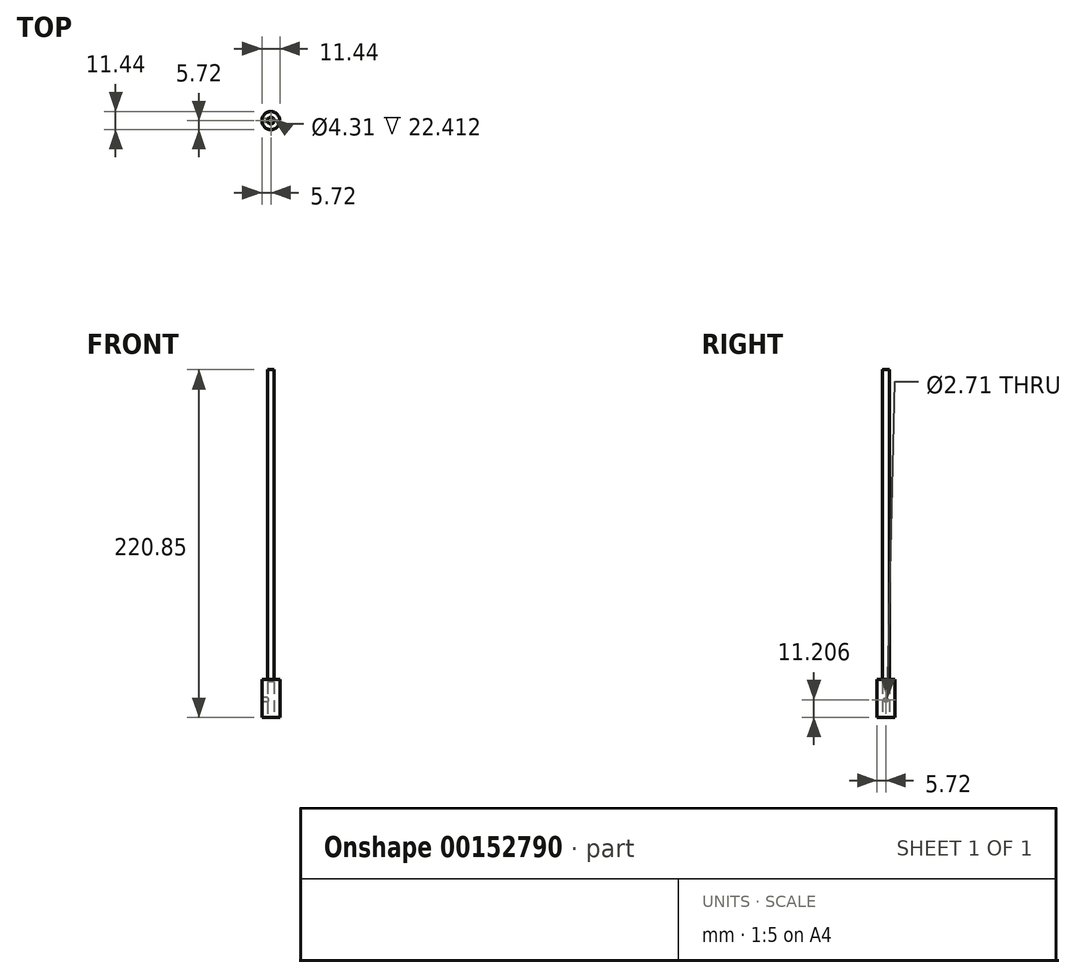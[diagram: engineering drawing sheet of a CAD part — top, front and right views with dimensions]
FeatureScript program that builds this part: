
annotation { "Feature Type Name" : "Feature", "Feature Type Description" : "" }
export const myFeature = defineFeature(function(context is Context, id is Id, definition is map)
    precondition{}
    {
        {
            var Q0;
            Q0=qCreatedBy(makeId("Top.planeOp"),FACE);
            var sketch = newSketch(context, id + "F0", { "sketchPlane" : qUnion([Q0])});
            skLineSegment(sketch, "E0.bottom", {"start": v(5.72, -5.72) * mm, "end": v(-5.72, -5.72) * mm});
            skLineSegment(sketch, "E0.top", {"start": v(5.72, 5.72) * mm, "end": v(-5.72, 5.71) * mm});
            skLineSegment(sketch, "E0.left", {"start": v(5.72, -5.72) * mm, "end": v(5.72, 5.72) * mm});
            skLineSegment(sketch, "E0.right", {"start": v(-5.72, -5.72) * mm, "end": v(-5.72, 5.71) * mm});
            skPoint(sketch, "E0.middle", {"position": v(0, 0) * mm});
            skCircle(sketch, "E1", {"center": v(0, 0) * mm, "radius": 5.72 * mm, "construction": true});
            skCircle(sketch, "E2", {"center": v(0, 0) * mm, "radius": 2.15 * mm});
            skLineSegment(sketch, "E3.bottom", {"start": v(2.15, 1.83) * mm, "end": v(5.41, 1.83) * mm, "construction": true});
            skLineSegment(sketch, "E3.top", {"start": v(2.15, -1.83) * mm, "end": v(5.41, -1.83) * mm, "construction": true});
            skLineSegment(sketch, "E3.left", {"start": v(2.15, 1.83) * mm, "end": v(2.15, -1.83) * mm, "construction": true});
            skLineSegment(sketch, "E3.right", {"start": v(5.41, 1.83) * mm, "end": v(5.41, -1.83) * mm, "construction": true});
            skLineSegment(sketch, "E4", {"start": v(2.15, 0) * mm, "end": v(0, 0) * mm, "construction": true});
            skSolve(sketch);
        }
        {
            var Q0;
            Q0 = qSketchRegion(id + "F0", true);
            extrude(context, id + "F1", {"entities" : qUnion([Q0]), "depth" : 22.41 * mm});
        }
        {
            var Q0;
            Q0=makeQuery(id+"F1.opExtrude","CAP_FACE",FACE,{"disambiguationData":[OSD([sQuery(id+"F0.wireOp",EDGE,"E0.bottom"),sQuery(id+"F0.wireOp",EDGE,"E0.top"),sQuery(id+"F0.wireOp",EDGE,"E0.left"),sQuery(id+"F0.wireOp",EDGE,"E0.right"),sQuery(id+"F0.wireOp",EDGE,"E2")])],"isStart":false});
            var sketch = newSketch(context, id + "F2", { "sketchPlane" : qUnion([Q0])});
            skLineSegment(sketch, "E5.bottom", {"start": v(-5.72, 5.71) * mm, "end": v(5.72, 5.71) * mm});
            skLineSegment(sketch, "E5.top", {"start": v(-5.72, -5.71) * mm, "end": v(5.72, -5.71) * mm});
            skLineSegment(sketch, "E5.left", {"start": v(-5.72, 5.71) * mm, "end": v(-5.72, -5.71) * mm});
            skLineSegment(sketch, "E5.right", {"start": v(5.72, 5.71) * mm, "end": v(5.72, -5.71) * mm});
            skPoint(sketch, "E5.middle", {"position": v(0, 0) * mm});
            skSolve(sketch);
        }
        {
            var Q0;
            Q0 = qSketchRegion(id + "F2", true);
            extrude(context, id + "F3", {"entities" : qUnion([Q0]), "operationType" : NewBodyOperationType.ADD, "depth" : 1.59 * mm});
        }
        {
            var Q0;
            Q0=makeQuery(id+"F70DsUOZgpewn3f_1.boolean.opBoolean","MERGE",FACE,{"derivedFrom":[makeQuery(id+"F3.boolean.opBoolean","MERGE",FACE,{"derivedFrom":[makeQuery(id+"F1.opExtrude","SWEPT_FACE",FACE,{"disambiguationData":[OSD([sQuery(id+"F0.wireOp",EDGE,"E0.right")])]}),makeQuery(id+"F3.opExtrude","SWEPT_FACE",FACE,{"disambiguationData":[OSD([sQuery(id+"F2.wireOp",EDGE,"E5.left")])]})]}),makeQuery(id+"F70DsUOZgpewn3f_1.opExtrude","SWEPT_FACE",FACE,{"disambiguationData":[OSD([sQuery(id+"FPdqaA84nfEKiEw_1.wireOp",EDGE,"Zp1nVK7z-LQDl-cVPR-DDhh-xMN3QgEcbA63.left")])]})]});
            var sketch = newSketch(context, id + "F4", { "sketchPlane" : qUnion([Q0])});
            skLineSegment(sketch, "E6", {"start": v(0, 0) * mm, "end": v(0, 22.41) * mm, "construction": true});
            skCircle(sketch, "E7", {"center": v(0, 11.2) * mm, "radius": 1.35 * mm});
            skSolve(sketch);
        }
        {
            var Q0;
            Q0 = qSketchRegion(id + "F4", true);
            var Q1;
            Q1=makeQuery(id+"F1.opExtrude","SWEPT_FACE",FACE,{"disambiguationData":[OSD([sQuery(id+"F0.wireOp",EDGE,"E2")])]});
            extrude(context, id + "F5", {"entities" : qUnion([Q0]), "operationType" : NewBodyOperationType.REMOVE, "endBound" : BoundingType.UP_TO_SURFACE, "oppositeDirection" : true, "endBoundEntityFace" : qUnion([Q1]), "depth" : 25.4 * mm});
        }
        {
            var Q0;
            Q0=makeQuery(id+"F70DsUOZgpewn3f_1.boolean.opBoolean","MERGE",EDGE,{"derivedFrom":[makeQuery(id+"F3.boolean.opBoolean","MERGE",EDGE,{"derivedFrom":[makeQuery(id+"F1.opExtrude","SWEPT_EDGE",EDGE,{"disambiguationData":[OSD([sQuery(id+"F0.wireOp",EDGE,"E0.top"),sQuery(id+"F0.wireOp",EDGE,"E0.right")])]}),makeQuery(id+"F3.opExtrude","SWEPT_EDGE",EDGE,{"disambiguationData":[OSD([sQuery(id+"F2.wireOp",EDGE,"E5.bottom"),sQuery(id+"F2.wireOp",EDGE,"E5.left")])]})]}),makeQuery(id+"F70DsUOZgpewn3f_1.opExtrude","SWEPT_EDGE",EDGE,{"disambiguationData":[OSD([sQuery(id+"FPdqaA84nfEKiEw_1.wireOp",EDGE,"Zp1nVK7z-LQDl-cVPR-DDhh-xMN3QgEcbA63.bottom"),sQuery(id+"FPdqaA84nfEKiEw_1.wireOp",EDGE,"Zp1nVK7z-LQDl-cVPR-DDhh-xMN3QgEcbA63.left")])]})]});
            var Q1;
            Q1=makeQuery(id+"F70DsUOZgpewn3f_1.boolean.opBoolean","MERGE",EDGE,{"derivedFrom":[makeQuery(id+"F3.boolean.opBoolean","MERGE",EDGE,{"derivedFrom":[makeQuery(id+"F1.opExtrude","SWEPT_EDGE",EDGE,{"disambiguationData":[OSD([sQuery(id+"F0.wireOp",EDGE,"E0.top"),sQuery(id+"F0.wireOp",EDGE,"E0.left")])]}),makeQuery(id+"F3.opExtrude","SWEPT_EDGE",EDGE,{"disambiguationData":[OSD([sQuery(id+"F2.wireOp",EDGE,"E5.bottom"),sQuery(id+"F2.wireOp",EDGE,"E5.right")])]})]}),makeQuery(id+"F70DsUOZgpewn3f_1.opExtrude","SWEPT_EDGE",EDGE,{"disambiguationData":[OSD([sQuery(id+"FPdqaA84nfEKiEw_1.wireOp",EDGE,"Zp1nVK7z-LQDl-cVPR-DDhh-xMN3QgEcbA63.bottom"),sQuery(id+"FPdqaA84nfEKiEw_1.wireOp",EDGE,"Zp1nVK7z-LQDl-cVPR-DDhh-xMN3QgEcbA63.right")])]})]});
            var Q2;
            Q2=makeQuery(id+"F70DsUOZgpewn3f_1.boolean.opBoolean","MERGE",EDGE,{"derivedFrom":[makeQuery(id+"F3.boolean.opBoolean","MERGE",EDGE,{"derivedFrom":[makeQuery(id+"F1.opExtrude","SWEPT_EDGE",EDGE,{"disambiguationData":[OSD([sQuery(id+"F0.wireOp",EDGE,"E0.bottom"),sQuery(id+"F0.wireOp",EDGE,"E0.right")])]}),makeQuery(id+"F3.opExtrude","SWEPT_EDGE",EDGE,{"disambiguationData":[OSD([sQuery(id+"F2.wireOp",EDGE,"E5.top"),sQuery(id+"F2.wireOp",EDGE,"E5.left")])]})]}),makeQuery(id+"F70DsUOZgpewn3f_1.opExtrude","SWEPT_EDGE",EDGE,{"disambiguationData":[OSD([sQuery(id+"FPdqaA84nfEKiEw_1.wireOp",EDGE,"Zp1nVK7z-LQDl-cVPR-DDhh-xMN3QgEcbA63.top"),sQuery(id+"FPdqaA84nfEKiEw_1.wireOp",EDGE,"Zp1nVK7z-LQDl-cVPR-DDhh-xMN3QgEcbA63.left")])]})]});
            var Q3;
            Q3=makeQuery(id+"F70DsUOZgpewn3f_1.boolean.opBoolean","MERGE",EDGE,{"derivedFrom":[makeQuery(id+"F3.boolean.opBoolean","MERGE",EDGE,{"derivedFrom":[makeQuery(id+"F1.opExtrude","SWEPT_EDGE",EDGE,{"disambiguationData":[OSD([sQuery(id+"F0.wireOp",EDGE,"E0.bottom"),sQuery(id+"F0.wireOp",EDGE,"E0.left")])]}),makeQuery(id+"F3.opExtrude","SWEPT_EDGE",EDGE,{"disambiguationData":[OSD([sQuery(id+"F2.wireOp",EDGE,"E5.top"),sQuery(id+"F2.wireOp",EDGE,"E5.right")])]})]}),makeQuery(id+"F70DsUOZgpewn3f_1.opExtrude","SWEPT_EDGE",EDGE,{"disambiguationData":[OSD([sQuery(id+"FPdqaA84nfEKiEw_1.wireOp",EDGE,"Zp1nVK7z-LQDl-cVPR-DDhh-xMN3QgEcbA63.top"),sQuery(id+"FPdqaA84nfEKiEw_1.wireOp",EDGE,"Zp1nVK7z-LQDl-cVPR-DDhh-xMN3QgEcbA63.right")])]})]});
            fillet(context, id + "F6", {"entities" : qUnion([Q0, Q1, Q2, Q3]), "radius" : 5.7 * mm, "tangentPropagation" : true, "allowEdgeOverflow" : false});
        }
        {
            var Q0;
            Q0=makeQuery(id+"F3.opExtrude","CAP_FACE",FACE,{"disambiguationData":[OSD([sQuery(id+"F2.wireOp",EDGE,"E5.bottom"),sQuery(id+"F2.wireOp",EDGE,"E5.top"),sQuery(id+"F2.wireOp",EDGE,"E5.left"),sQuery(id+"F2.wireOp",EDGE,"E5.right")])],"isStart":false});
            var sketch = newSketch(context, id + "F7", { "sketchPlane" : qUnion([Q0])});
            skCircle(sketch, "E8", {"center": v(0, 0) * mm, "radius": 2.15 * mm});
            skSolve(sketch);
        }
        {
            var Q0;
            Q0 = qSketchRegion(id + "F7", true);
            extrude(context, id + "F8", {"entities" : qUnion([Q0]), "operationType" : NewBodyOperationType.ADD, "depth" : 196.85 * mm});
        }
    });
